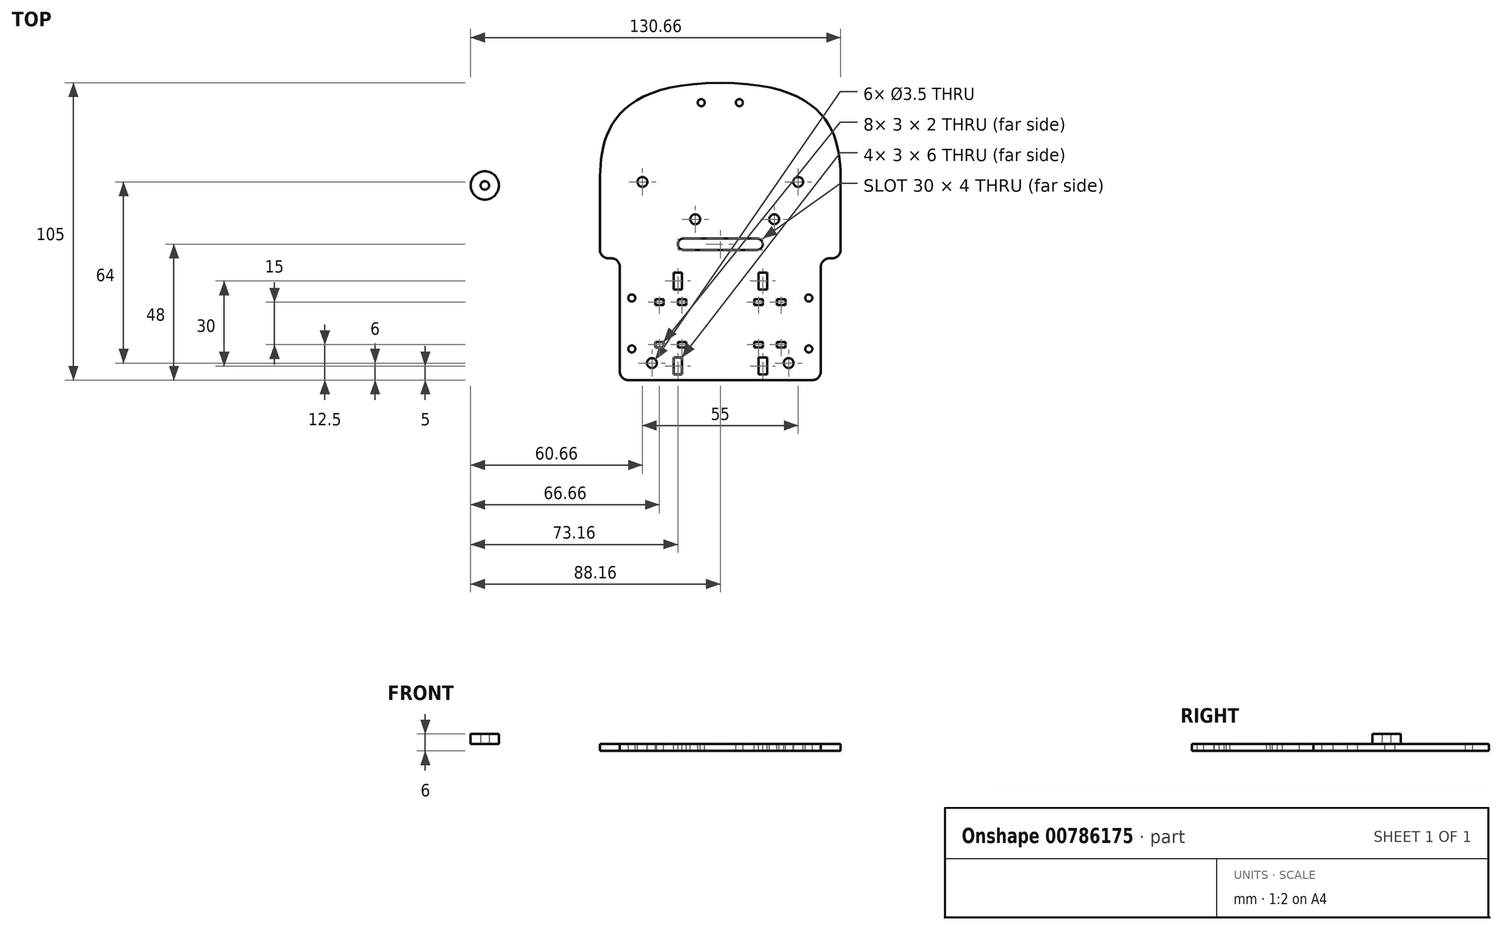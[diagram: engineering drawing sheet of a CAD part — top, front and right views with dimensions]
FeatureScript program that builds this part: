
annotation { "Feature Type Name" : "Feature", "Feature Type Description" : "" }
export const myFeature = defineFeature(function(context is Context, id is Id, definition is map)
    precondition{}
    {
        {
            var Q0;
            Q0=qCreatedBy(makeId("Top.planeOp"),FACE);
            var sketch = newSketch(context, id + "F0", { "sketchPlane" : qUnion([Q0])});
            skPoint(sketch, "E0.middle", {"position": v(0, 0) * mm});
            skLineSegment(sketch, "E1", {"start": v(4.5, 6) * mm, "end": v(31.5, 6) * mm});
            skLineSegment(sketch, "E2", {"start": v(31.5, 6) * mm, "end": v(31.5, -6) * mm});
            skLineSegment(sketch, "E3", {"start": v(31.5, -6) * mm, "end": v(5.5, -6) * mm});
            skLineSegment(sketch, "E4.bottom", {"start": v(20, 6.5) * mm, "end": v(17, 6.5) * mm});
            skLineSegment(sketch, "E4.top", {"start": v(20, 8.5) * mm, "end": v(17, 8.5) * mm});
            skLineSegment(sketch, "E4.left", {"start": v(20, 6.5) * mm, "end": v(20, 8.5) * mm});
            skLineSegment(sketch, "E4.right", {"start": v(17, 6.5) * mm, "end": v(17, 8.5) * mm});
            skPoint(sketch, "E4.middle", {"position": v(18.5, 7.5) * mm});
            skLineSegment(sketch, "E5.bottom", {"start": v(25, 8.5) * mm, "end": v(28, 8.5) * mm});
            skLineSegment(sketch, "E5.top", {"start": v(25, 6.5) * mm, "end": v(28, 6.5) * mm});
            skLineSegment(sketch, "E5.left", {"start": v(25, 8.5) * mm, "end": v(25, 6.5) * mm});
            skLineSegment(sketch, "E5.right", {"start": v(28, 8.5) * mm, "end": v(28, 6.5) * mm});
            skPoint(sketch, "E5.middle", {"position": v(26.5, 7.5) * mm});
            skLineSegment(sketch, "E6", {"start": v(40, -20) * mm, "end": v(40, -20) * mm});
            skLineSegment(sketch, "E7.bottom", {"start": v(26.5, -12) * mm, "end": v(23.5, -12) * mm});
            skLineSegment(sketch, "E7.top", {"start": v(26.5, -18) * mm, "end": v(23.5, -18) * mm});
            skLineSegment(sketch, "E7.left", {"start": v(26.5, -12) * mm, "end": v(26.5, -18) * mm});
            skLineSegment(sketch, "E7.right", {"start": v(23.5, -12) * mm, "end": v(23.5, -18) * mm});
            skPoint(sketch, "E7.middle", {"position": v(25, -15) * mm});
            skLineSegment(sketch, "E8.bottom", {"start": v(23.5, 12) * mm, "end": v(26.5, 12) * mm});
            skLineSegment(sketch, "E8.top", {"start": v(23.5, 18) * mm, "end": v(26.5, 18) * mm});
            skLineSegment(sketch, "E8.left", {"start": v(23.5, 12) * mm, "end": v(23.5, 18) * mm});
            skLineSegment(sketch, "E8.right", {"start": v(26.5, 12) * mm, "end": v(26.5, 18) * mm});
            skPoint(sketch, "E8.middle", {"position": v(25, 15) * mm});
            skCircle(sketch, "E9", {"center": v(8.75, 9) * mm, "radius": 1.25 * mm});
            skCircle(sketch, "E10", {"center": v(8.75, -9) * mm, "radius": 1.25 * mm});
            skCircle(sketch, "E11", {"center": v(12.5, 50) * mm, "radius": 1.75 * mm});
            skLineSegment(sketch, "E12", {"start": v(0.5, 23) * mm, "end": v(1.5, 23) * mm});
            skLineSegment(sketch, "E13", {"start": v(4.5, 20) * mm, "end": v(4.5, -17) * mm});
            skLineSegment(sketch, "E14", {"start": v(7.5, -20) * mm, "end": v(40, -20) * mm});
            skLineSegment(sketch, "E15", {"start": v(40, 85) * mm, "end": v(-2.5, 85) * mm});
            skLineSegment(sketch, "E16", {"start": v(-2.5, 85) * mm, "end": v(-2.5, 26) * mm});
            skLineSegment(sketch, "E17", {"start": v(40, -20) * mm, "end": v(40, 85) * mm, "construction": true});
            skLineSegment(sketch, "E18", {"start": v(7.5, 60) * mm, "end": v(7.5, 65) * mm});
            skLineSegment(sketch, "E19", {"start": v(12.5, 70) * mm, "end": v(40, 70) * mm});
            skLineSegment(sketch, "E20", {"start": v(19.5, 48) * mm, "end": v(40, 48) * mm});
            skLineSegment(sketch, "E21", {"start": v(17.5, 50) * mm, "end": v(17.5, 50) * mm});
            skLineSegment(sketch, "E22", {"start": v(12.5, 55) * mm, "end": v(12.5, 55) * mm});
            skCircle(sketch, "E23", {"center": v(33.27, 78) * mm, "radius": 1.25 * mm});
            skPoint(sketch, "E24.visualSharp", {"position": v(7.5, 70) * mm});
            skArc(sketch, "E24.filletArc", {"start": v(12.5, 70) * mm, "mid": v(8.96, 68.54) * mm, "end": v(7.5, 65) * mm});
            skPoint(sketch, "E25.visualSharp", {"position": v(7.5, 55) * mm});
            skArc(sketch, "E25.filletArc", {"start": v(7.5, 60) * mm, "mid": v(8.96, 56.46) * mm, "end": v(12.5, 55) * mm});
            skPoint(sketch, "E26.visualSharp", {"position": v(17.5, 55) * mm});
            skArc(sketch, "E26.filletArc", {"start": v(17.5, 50) * mm, "mid": v(16.04, 53.54) * mm, "end": v(12.5, 55) * mm});
            skPoint(sketch, "E27.visualSharp", {"position": v(17.5, 48) * mm});
            skArc(sketch, "E27.filletArc", {"start": v(17.5, 50) * mm, "mid": v(18.09, 48.59) * mm, "end": v(19.5, 48) * mm});
            skPoint(sketch, "E28.visualSharp", {"position": v(-2.5, 23) * mm});
            skArc(sketch, "E28.filletArc", {"start": v(-2.5, 26) * mm, "mid": v(-1.62, 23.88) * mm, "end": v(0.5, 23) * mm});
            skPoint(sketch, "E29.visualSharp", {"position": v(4.5, 23) * mm});
            skArc(sketch, "E29.filletArc", {"start": v(4.5, 20) * mm, "mid": v(3.62, 22.12) * mm, "end": v(1.5, 23) * mm});
            skPoint(sketch, "E30.visualSharp", {"position": v(4.5, -20) * mm});
            skArc(sketch, "E30.filletArc", {"start": v(4.5, -17) * mm, "mid": v(5.38, -19.12) * mm, "end": v(7.5, -20) * mm});
            skCircle(sketch, "E31", {"center": v(15.85, -14) * mm, "radius": 1.75 * mm});
            skCircle(sketch, "E32", {"center": v(64.15, -14) * mm, "radius": 1.75 * mm});
            skCircle(sketch, "E33", {"center": v(59.05, 36.8) * mm, "radius": 1.75 * mm});
            skCircle(sketch, "E34", {"center": v(31.15, 36.8) * mm, "radius": 1.75 * mm});
            skLineSegment(sketch, "E35.bottom", {"start": v(-2.5, -20) * mm, "end": v(2.5, -20) * mm});
            skLineSegment(sketch, "E35.top", {"start": v(-2.5, 20) * mm, "end": v(2.5, 20) * mm});
            skLineSegment(sketch, "E35.left", {"start": v(-2.5, -20) * mm, "end": v(-2.5, 20) * mm});
            skLineSegment(sketch, "E35.right", {"start": v(2.5, -20) * mm, "end": v(2.5, 20) * mm});
            skLineSegment(sketch, "E36", {"start": v(0, 0) * mm, "end": v(100, 0) * mm, "construction": true});
            skLineSegment(sketch, "E37.bottom", {"start": v(28, -6.5) * mm, "end": v(25, -6.5) * mm});
            skLineSegment(sketch, "E37.top", {"start": v(28, -8.5) * mm, "end": v(25, -8.5) * mm});
            skLineSegment(sketch, "E37.left", {"start": v(28, -6.5) * mm, "end": v(28, -8.5) * mm});
            skLineSegment(sketch, "E37.right", {"start": v(25, -6.5) * mm, "end": v(25, -8.5) * mm});
            skPoint(sketch, "E37.middle", {"position": v(26.5, -7.5) * mm});
            skLineSegment(sketch, "E38.bottom", {"start": v(20, -6.5) * mm, "end": v(17, -6.5) * mm});
            skLineSegment(sketch, "E38.top", {"start": v(20, -8.5) * mm, "end": v(17, -8.5) * mm});
            skLineSegment(sketch, "E38.left", {"start": v(20, -6.5) * mm, "end": v(20, -8.5) * mm});
            skLineSegment(sketch, "E38.right", {"start": v(17, -6.5) * mm, "end": v(17, -8.5) * mm});
            skPoint(sketch, "E38.middle", {"position": v(18.5, -7.5) * mm});
            skPoint(sketch, "E38.middle.positionSnap0", {"position": v(18.5, 6.5) * mm});
            skPoint(sketch, "E38.centerSnap0", {"position": v(18.5, 6.5) * mm});
            skFitSpline(sketch, "E39", {"points": [v(40, 85) * mm, v(-2.5, 50) * mm], "startDerivative": vector(-120, 0) * mm, "endDerivative": vector(0, -45) * mm});
            skLineSegment(sketch, "E40", {"start": v(40, 30) * mm, "end": v(27, 30) * mm});
            skLineSegment(sketch, "E41", {"start": v(25, 28) * mm, "end": v(25, 28) * mm});
            skLineSegment(sketch, "E42", {"start": v(27, 26) * mm, "end": v(40, 26) * mm});
            skPoint(sketch, "E43.visualSharp", {"position": v(25, 26) * mm});
            skArc(sketch, "E43.filletArc", {"start": v(25, 28) * mm, "mid": v(25.59, 26.59) * mm, "end": v(27, 26) * mm});
            skPoint(sketch, "E44.visualSharp", {"position": v(25, 30) * mm});
            skArc(sketch, "E44.filletArc", {"start": v(27, 30) * mm, "mid": v(25.59, 29.41) * mm, "end": v(25, 28) * mm});
            skArc(sketch, "E45.MirrorCS", {"start": v(82.5, 26) * mm, "mid": v(81.62, 23.88) * mm, "end": v(79.5, 23) * mm});
            skArc(sketch, "E46.MirrorCS", {"start": v(75.5, 20) * mm, "mid": v(76.38, 22.12) * mm, "end": v(78.5, 23) * mm});
            skLineSegment(sketch, "E47.MirrorCS", {"start": v(82.5, 20) * mm, "end": v(77.5, 20) * mm});
            skArc(sketch, "E48.MirrorCS", {"start": v(53, 30) * mm, "mid": v(54.41, 29.41) * mm, "end": v(55, 28) * mm});
            skLineSegment(sketch, "E49.MirrorCS", {"start": v(60, 6.5) * mm, "end": v(63, 6.5) * mm});
            skLineSegment(sketch, "E50.MirrorCS", {"start": v(55, -6.5) * mm, "end": v(55, -8.5) * mm});
            skLineSegment(sketch, "E51.MirrorCS", {"start": v(60, 8.5) * mm, "end": v(63, 8.5) * mm});
            skLineSegment(sketch, "E52.MirrorCS", {"start": v(60, 6.5) * mm, "end": v(60, 8.5) * mm});
            skArc(sketch, "E53.MirrorCS", {"start": v(55, 28) * mm, "mid": v(54.41, 26.59) * mm, "end": v(53, 26) * mm});
            skLineSegment(sketch, "E54.MirrorCS", {"start": v(55, 8.5) * mm, "end": v(55, 6.5) * mm});
            skLineSegment(sketch, "E55.MirrorCS", {"start": v(60, -6.5) * mm, "end": v(60, -8.5) * mm});
            skLineSegment(sketch, "E56.MirrorCS", {"start": v(63, 6.5) * mm, "end": v(63, 8.5) * mm});
            skLineSegment(sketch, "E57.MirrorCS", {"start": v(52, 8.5) * mm, "end": v(52, 6.5) * mm});
            skLineSegment(sketch, "E58.MirrorCS", {"start": v(52, -8.5) * mm, "end": v(55, -8.5) * mm});
            skLineSegment(sketch, "E59.MirrorCS", {"start": v(56.5, 18) * mm, "end": v(53.5, 18) * mm});
            skLineSegment(sketch, "E60.MirrorCS", {"start": v(53.5, -12) * mm, "end": v(56.5, -12) * mm});
            skLineSegment(sketch, "E61.MirrorCS", {"start": v(60, -8.5) * mm, "end": v(63, -8.5) * mm});
            skLineSegment(sketch, "E62.MirrorCS", {"start": v(63, -6.5) * mm, "end": v(63, -8.5) * mm});
            skLineSegment(sketch, "E63.MirrorCS", {"start": v(56.5, 12) * mm, "end": v(53.5, 12) * mm});
            skLineSegment(sketch, "E64.MirrorCS", {"start": v(60, -6.5) * mm, "end": v(63, -6.5) * mm});
            skLineSegment(sketch, "E65.MirrorCS", {"start": v(53.5, 12) * mm, "end": v(53.5, 18) * mm});
            skArc(sketch, "E66.MirrorCS", {"start": v(75.5, -17) * mm, "mid": v(74.62, -19.12) * mm, "end": v(72.5, -20) * mm});
            skLineSegment(sketch, "E67.MirrorCS", {"start": v(55, 8.5) * mm, "end": v(52, 8.5) * mm});
            skLineSegment(sketch, "E68.MirrorCS", {"start": v(55, 6.5) * mm, "end": v(52, 6.5) * mm});
            skLineSegment(sketch, "E69.MirrorCS", {"start": v(52, -6.5) * mm, "end": v(55, -6.5) * mm});
            skLineSegment(sketch, "E70.MirrorCS", {"start": v(56.5, 12) * mm, "end": v(56.5, 18) * mm});
            skArc(sketch, "E71.MirrorCS", {"start": v(62.5, 50) * mm, "mid": v(63.96, 53.54) * mm, "end": v(67.5, 55) * mm});
            skLineSegment(sketch, "E72.MirrorCS", {"start": v(52, -6.5) * mm, "end": v(52, -8.5) * mm});
            skLineSegment(sketch, "E73.MirrorCS", {"start": v(67.5, 55) * mm, "end": v(67.5, 55) * mm});
            skCircle(sketch, "E74.MirrorC", {"center": v(67.5, 50) * mm, "radius": 1.75 * mm});
            skLineSegment(sketch, "E75.MirrorCS", {"start": v(53.5, -18) * mm, "end": v(56.5, -18) * mm});
            skLineSegment(sketch, "E76.MirrorCS", {"start": v(56.5, -12) * mm, "end": v(56.5, -18) * mm});
            skLineSegment(sketch, "E77.MirrorCS", {"start": v(75.5, 6) * mm, "end": v(48.5, 6) * mm});
            skCircle(sketch, "E78.MirrorC", {"center": v(71.25, 9) * mm, "radius": 1.25 * mm});
            skArc(sketch, "E79.MirrorCS", {"start": v(67.5, 70) * mm, "mid": v(71.04, 68.54) * mm, "end": v(72.5, 65) * mm});
            skLineSegment(sketch, "E80.MirrorCS", {"start": v(53.5, -12) * mm, "end": v(53.5, -18) * mm});
            skLineSegment(sketch, "E81.MirrorCS", {"start": v(82.5, -20) * mm, "end": v(77.5, -20) * mm});
            skCircle(sketch, "E82.MirrorC", {"center": v(71.25, -9) * mm, "radius": 1.25 * mm});
            skArc(sketch, "E83.MirrorCS", {"start": v(72.5, 60) * mm, "mid": v(71.04, 56.46) * mm, "end": v(67.5, 55) * mm});
            skArc(sketch, "E84.MirrorCS", {"start": v(62.5, 50) * mm, "mid": v(61.91, 48.59) * mm, "end": v(60.5, 48) * mm});
            skLineSegment(sketch, "E85.MirrorCS", {"start": v(75.5, 20) * mm, "end": v(75.5, -17) * mm});
            skLineSegment(sketch, "E86.MirrorCS", {"start": v(48.5, 6) * mm, "end": v(48.5, -6) * mm});
            skPoint(sketch, "E87.MirrorP", {"position": v(61.5, 6.5) * mm});
            skPoint(sketch, "E88.MirrorP", {"position": v(80, 0) * mm});
            skLineSegment(sketch, "E89.MirrorCS", {"start": v(53, 26) * mm, "end": v(40, 26) * mm});
            skLineSegment(sketch, "E90.MirrorCS", {"start": v(77.5, -20) * mm, "end": v(77.5, 20) * mm});
            skLineSegment(sketch, "E91.MirrorCS", {"start": v(48.5, -6) * mm, "end": v(74.5, -6) * mm});
            skCircle(sketch, "E92.MirrorC", {"center": v(46.73, 78) * mm, "radius": 1.25 * mm});
            skLineSegment(sketch, "E93.MirrorCS", {"start": v(72.5, 60) * mm, "end": v(72.5, 65) * mm});
            skPoint(sketch, "E94.MirrorP", {"position": v(53.5, -7.5) * mm});
            skPoint(sketch, "E95.MirrorP", {"position": v(55, 26) * mm});
            skFitSpline(sketch, "E96.MirrorCS", {"points": [v(40, 85) * mm, v(82.5, 50) * mm], "startDerivative": vector(120, 0) * mm, "endDerivative": vector(0, -45) * mm});
            skPoint(sketch, "E97.MirrorP", {"position": v(55, 30) * mm});
            skLineSegment(sketch, "E98.MirrorCS", {"start": v(40, 30) * mm, "end": v(53, 30) * mm});
            skPoint(sketch, "E99.MirrorP", {"position": v(72.5, 70) * mm});
            skLineSegment(sketch, "E100.MirrorCS", {"start": v(72.5, -20) * mm, "end": v(40, -20) * mm});
            skLineSegment(sketch, "E101.MirrorCS", {"start": v(60.5, 48) * mm, "end": v(40, 48) * mm});
            skPoint(sketch, "E102.MirrorP", {"position": v(82.5, 23) * mm});
            skPoint(sketch, "E103.MirrorP", {"position": v(61.5, 7.5) * mm});
            skLineSegment(sketch, "E104.MirrorCS", {"start": v(82.5, -20) * mm, "end": v(82.5, 20) * mm});
            skPoint(sketch, "E105.MirrorP", {"position": v(62.5, 48) * mm});
            skPoint(sketch, "E106.MirrorP", {"position": v(75.5, -20) * mm});
            skPoint(sketch, "E107.MirrorP", {"position": v(53.5, 7.5) * mm});
            skLineSegment(sketch, "E108.MirrorCS", {"start": v(67.5, 70) * mm, "end": v(40, 70) * mm});
            skPoint(sketch, "E109.MirrorP", {"position": v(72.5, 55) * mm});
            skPoint(sketch, "E110.MirrorP", {"position": v(62.5, 55) * mm});
            skPoint(sketch, "E111.MirrorP", {"position": v(55, 15) * mm});
            skPoint(sketch, "E112.MirrorP", {"position": v(75.5, 23) * mm});
            skPoint(sketch, "E113.MirrorP", {"position": v(61.5, -7.5) * mm});
            skPoint(sketch, "E114.MirrorP", {"position": v(55, -15) * mm});
            skLineSegment(sketch, "E115.MirrorCS", {"start": v(40, 85) * mm, "end": v(82.5, 85) * mm});
            skLineSegment(sketch, "E116", {"start": v(82.5, 26) * mm, "end": v(82.5, 50) * mm});
            skPoint(sketch, "E117", {"position": v(18.5, -6) * mm});
            skLineSegment(sketch, "E118", {"start": v(5.5, -6) * mm, "end": v(4.5, -6) * mm});
            skLineSegment(sketch, "E119", {"start": v(74.5, -6) * mm, "end": v(75.5, -6) * mm});
            skLineSegment(sketch, "E120", {"start": v(79.5, 23) * mm, "end": v(78.5, 23) * mm});
            skSolve(sketch);
        }
        {
            var Q0;
            {var subQ1=sQuery(id+"F0.wireOp",EDGE,"E1");Q0=makeQuery(id+"F0.imprint","IMPRINT",FACE,{"disambiguationData":[TD([[makeQuery(id+"F0.imprint","IMPRINT",EDGE,{"derivedFrom":subQ1}),-1.0]])]});}
            var Q1;
            {var subQ0=sQuery(id+"F0.wireOp",EDGE,"E77.MirrorCS");Q1=makeQuery(id+"F0.imprint","IMPRINT",FACE,{"disambiguationData":[TD([[makeQuery(id+"F0.imprint","IMPRINT",EDGE,{"derivedFrom":subQ0}),1.0]])]});}
            var Q2;
            Q2=makeQuery(id+"F0.imprint","IMPRINT",FACE,{"disambiguationData":[TD([[makeQuery(id+"F0.imprint","IMPRINT",EDGE,{"derivedFrom":sQuery(id+"F0.wireOp",EDGE,"E18")}),-1.0]])]});
            var Q3;
            {var subQ4=sQuery(id+"F0.wireOp",EDGE,"E1");Q3=makeQuery(id+"F0.imprint","IMPRINT",FACE,{"disambiguationData":[TD([[makeQuery(id+"F0.imprint","IMPRINT",EDGE,{"derivedFrom":subQ4}),1.0]])]});}
            extrude(context, id + "F1", {"entities" : qUnion([Q0, Q1, Q2, Q3]), "oppositeDirection" : true, "depth" : 2.5 * mm, "offsetDistance" : 25 * mm});
        }
        {
            var Q0;
            Q0=qCreatedBy(makeId("Top.planeOp"),FACE);
            var sketch = newSketch(context, id + "F2", { "sketchPlane" : qUnion([Q0])});
            skCircle(sketch, "E121", {"center": v(-43.16, 48.77) * mm, "radius": 1.5 * mm});
            skCircle(sketch, "E122", {"center": v(-43.16, 48.77) * mm, "radius": 5 * mm});
            skSolve(sketch);
        }
        {
            var Q0;
            Q0=makeQuery(id+"F2.imprint","IMPRINT",FACE,{"disambiguationData":[TD([[makeQuery(id+"F2.imprint","IMPRINT",EDGE,{"derivedFrom":sQuery(id+"F2.wireOp",EDGE,"E121")}),-1.0]])]});
            extrude(context, id + "F3", {"entities" : qUnion([Q0]), "depth" : 3.5 * mm, "offsetDistance" : 25 * mm});
        }
    });
